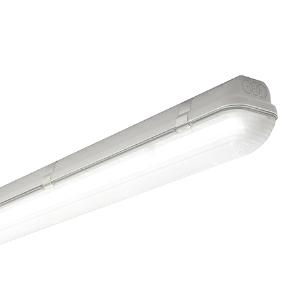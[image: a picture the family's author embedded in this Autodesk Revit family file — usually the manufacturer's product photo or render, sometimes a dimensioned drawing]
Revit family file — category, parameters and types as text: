
# Revit family: 3f_filippi_-_3f_linda_soft_3f_filippi_-_58734_-_3f_linda_led_soft_1x30w_l1570
name_source: partatom
category: Lighting Fixtures
units: mm (PartAtom-declared; Revit-internal decimal feet)

## family parameters
Cut with Voids When Loaded = No
Host = Face
Light Source = No
Part Type = Normal
Room Calculation Point = No
Round Connector Dimension = Use Diameter
Shared = No

## types (1)
- 3F Filippi - 3F Linda Soft (1 x LED, 4755 lm, 33.5 W, 4000 K)
    Apparent Load = 34 VA
    Approval mark = CE
    CIE Flux Codes = 39 68 88 89 100
    Color Rendering = 80
    Color Temperature = 4000 K
    Control Gear = Electronic ballast
    Default Elevation = 1800 mm
    Description = ILLUMINOTECHNICAL
Luminous efficiency 100% (DLOR 89%, ULOR 11%).
Initial luminous flux of the luminaire 4755 lm.
Direct symmetric distribution.
Installation Interdistance Transv.D = 1.39 x hu - Long.D = 1.21 x hu.
Tabular UGR (CIE 117 - 4H-8H; S=0.25H; 70/50/20): RUG 24 - 21.
Beam angle: 149° - 108°.
Luminous efficacy 142 lm/W.
Lifetime (L93/B10): 30000 h. (tq+25°C)
Lifetime (L90/B10): 50000 h. (tq+25°C)
Lifetime (L85/B10): 80000 h. (tq+25°C)
Lifetime (L80/B10): 100000 h. (tq+25°C)
Lifetime (L85/B10): 50000 h. (tq+35°C)
Sudden decreased luminous flux after 50000 hours: 0% (C0).
Photobiological safety in compliance with IEC/TR 62778: RG0 risk exempt, (IEC 62471).
In compliance with IEC/EN 62722-2-1 - IEC/EN 62717 standards.

SOURCE
Linear LED module 30W/840.
Energy efficiency class (UE 2019/2020 - UE 2019/2015): D.
CIE 13.3 Colour rendering index: CRI >80 (R9 <50%).
IES TM-30 Fidelity Index: Rf = 84 Rg = 95.
CCT nominal colour temperature 4000 K.
Colour initial tolerance (MacAdam): SDCM 3.

MECHANICAL
Self-extinguishing V2 polycarbonate housing, injection moulded, RAL 7035 grey.
Ecologic anti-aging injected sealing gasket.
Soft opal diffuser in self-extinguishing V2 polycarbonate, photo-engraved interior, UV stabilised, injection moulded.
Gear-holder reflector in hot-dip galvanised steel, painted with white polyester base.
Snug fit safety snap-lock clips for diffuser mounting in stainless steel, screwdriver opening.
Fixing brackets in stainless steel.
Possibility for technicians to access the interior of the luminaire.
Luminaire with limited surface temperature. - D - (EN 60598-2-24)
Dimensions: 1570x100 mm, height 100 mm. Weight 2.485 kg.
IP66 protection degree.
Mechanical strength to impacts IK10 (20 joule).
Glow-wire test resistance 850°C.

ELECTRICAL
Halogen Free electronic wiring 230V-50/60Hz, power factor 0.95, THD <25%, constant output current, SELV, class I, 1 driver.
Power of the luminaire 33.5 W.
ENEC - CE.
SAFE FLICKER: PstLM=<1 and SVM=<0.4 (IEC TR 61547-1 and IEC TR 63158), to ensure a more comfortable and safe light.
Luminaire compliant with EN 60598-2-22 for power supply from a centralised emergency system CPSS (Central Power Supply System), not incorporated in the luminaire - high risk areas excluded. The default power and flux are 100% in AC and 100% in DC.
Ambient temperature from -20°C to +35°C.
Temperature class T6 max 85°C.
Relative humidity UR: <85%.

INSTALLATION
Ceiling / Suspended / Wall.
All accessories dedicated to this product are available on the Catalog and on our website www.3F-Filippi.com.

APPLICATIONS
Suitable product for food production plants (HACCP), IFS (Food Version 6), BRC (GSFS Food Version 7).
Dry, dusty indoor environments, subject to occasional water splashes.
Luminaires designed for diffuse direct/indirect lighting suitable to provide optimum visual comfort.
Transit areas, stairwells.
Virtually shatterproof polycarbonate compatibly with the fumes / atmospheres that compromise the elasticity of plastic materials.
Suitable for illumination of public car parks and parking grounds referred to DIN 67528:2018-04.

WARNING
Fixture not suitable for cold stores with an ambient temperature <0°C and/or relative humidity >85%.
Luminaire designed for disposal/recycling at end-of-life.
Replaceable (LED only) light source by a professional. Replaceable control gear by a professional.
    Height = 100 mm  [stored 0.328084 ft]
    Lamp = 1 x LED
    Lamp Light Flux = 4755 lm
    Lamp Power = 33.5 W
    Lamp count = 1
    Length = 1570 mm
    Lifetime = 50000 h
    Luminous efficacy = 142 lm/W
    Manufacturer = 3F Filippi
    ModVariant = No
    Model = 3F Filippi - 58734 - 3F Linda LED Soft 1x30W L1570
    Mounting Place = Ceiling
    Mounting Type = Pendant
    Number of Poles = 1
    OnlyDefault = Yes
    Power Factor = 1
    Product Name = 3F Filippi - 3F Linda Soft
    Product group = pendant luminaire
    ProductGroupID = 9
    Protection Class = Protection class I
    Protection Degree = IP 66
    RLX_Detail_Level = 1
    RLX_Emergency_Light_Flux = 0 lm
    RLX_Emergency_Type = 0
    RLX_Emergency_Type_DB = No
    RlxData = <blob elided: 59389 chars, md5=d4496084>
    Socket = socket
    Standby Power = 0 W
    System Light Flux = 4755 lm
    System Power = 34 W
    Type Comments = Product without accessories
    Type Image = 3ffilippi_3f_linda_led_soft_1x.jpg
    URL = http://relux.com
    VarID = ---
    Voltage = 0 V
    Weight = 0.00 kg
    Width = 100 mm  [stored 0.328084 ft]

note: [stored X ft] marks values corroborated as IEEE doubles in the binary element streams (Revit-internal decimal feet)

## geometry (parser evidence)
native form markers: Blend x4, Sweep x12
no freeform markers — native parametric forms only
